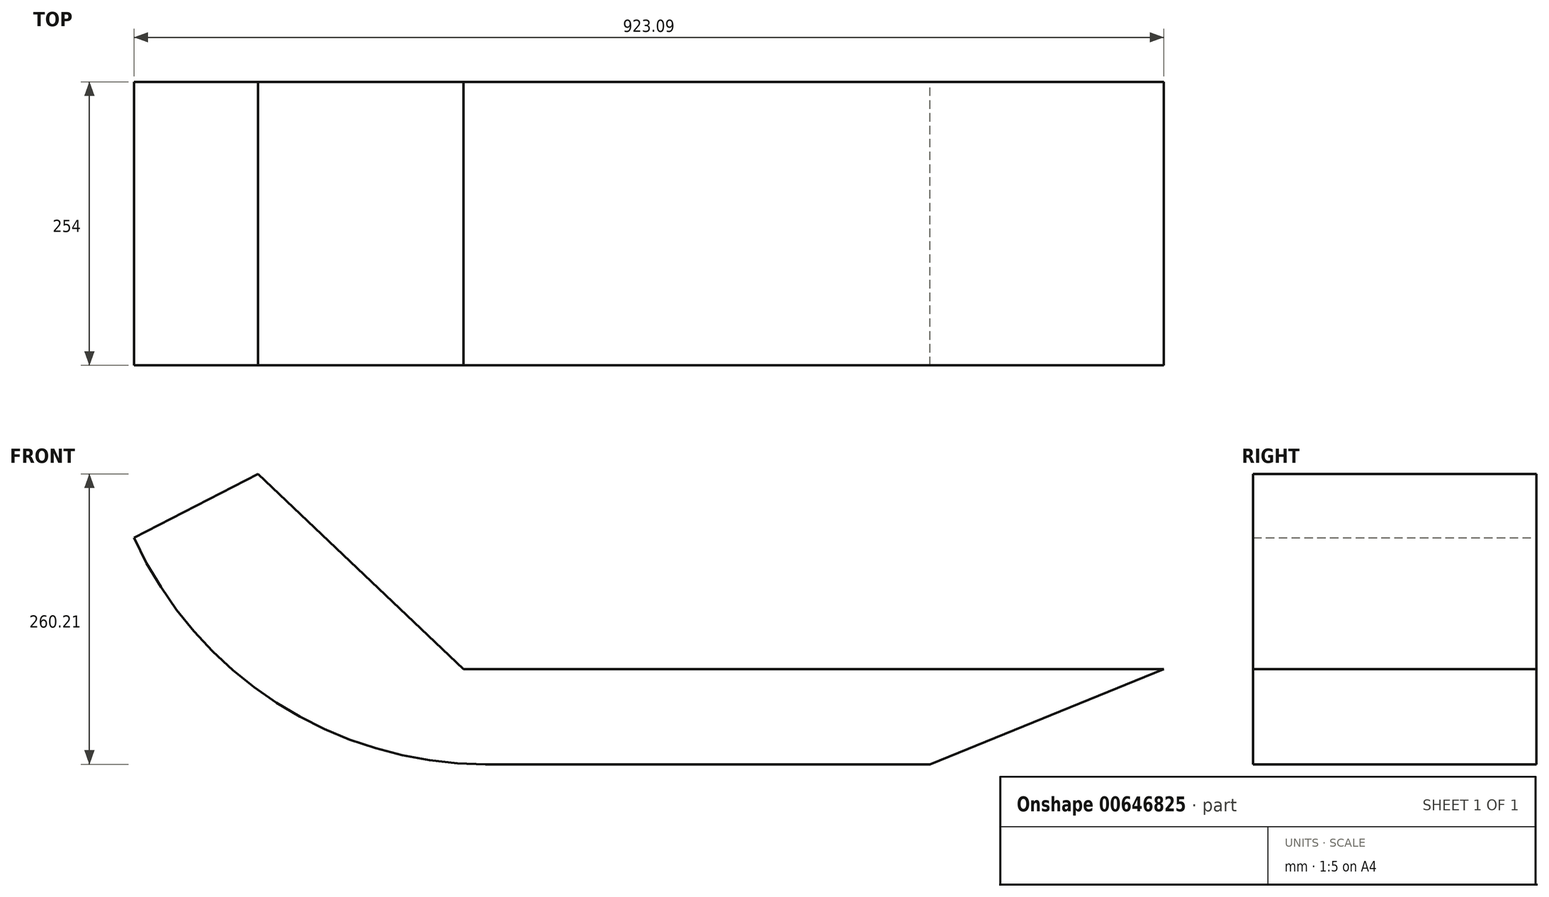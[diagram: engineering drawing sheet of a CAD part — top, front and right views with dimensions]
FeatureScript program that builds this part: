
annotation { "Feature Type Name" : "Feature", "Feature Type Description" : "" }
export const myFeature = defineFeature(function(context is Context, id is Id, definition is map)
    precondition{}
    {
        {
            var Q0;
            Q0=qCreatedBy(makeId("Front.planeOp"),FACE);
            var sketch = newSketch(context, id + "F0", { "sketchPlane" : qUnion([Q0])});
            skLineSegment(sketch, "E0", {"start": v(-510.04, 148.54) * mm, "end": v(-399, 205.74) * mm});
            skLineSegment(sketch, "E1", {"start": v(-399, 205.74) * mm, "end": v(-214.76, 30.77) * mm});
            skLineSegment(sketch, "E2", {"start": v(-214.76, 30.77) * mm, "end": v(413.05, 30.77) * mm});
            skLineSegment(sketch, "E3", {"start": v(413.05, 30.77) * mm, "end": v(203.3, -54.47) * mm});
            skLineSegment(sketch, "E4", {"start": v(203.3, -54.47) * mm, "end": v(-194.86, -54.47) * mm});
            skArc(sketch, "E5", {"start": v(-510.04, 148.54) * mm, "mid": v(-382.31, 0.67) * mm, "end": v(-194.86, -54.47) * mm});
            skSolve(sketch);
        }
        {
            var Q0;
            Q0 = qSketchRegion(id + "F0", true);
            extrude(context, id + "F1", {"entities" : qUnion([Q0]), "endBound" : BoundingType.SYMMETRIC, "depth" : 254 * mm, "offsetDistance" : 25.4 * mm});
        }
    });
